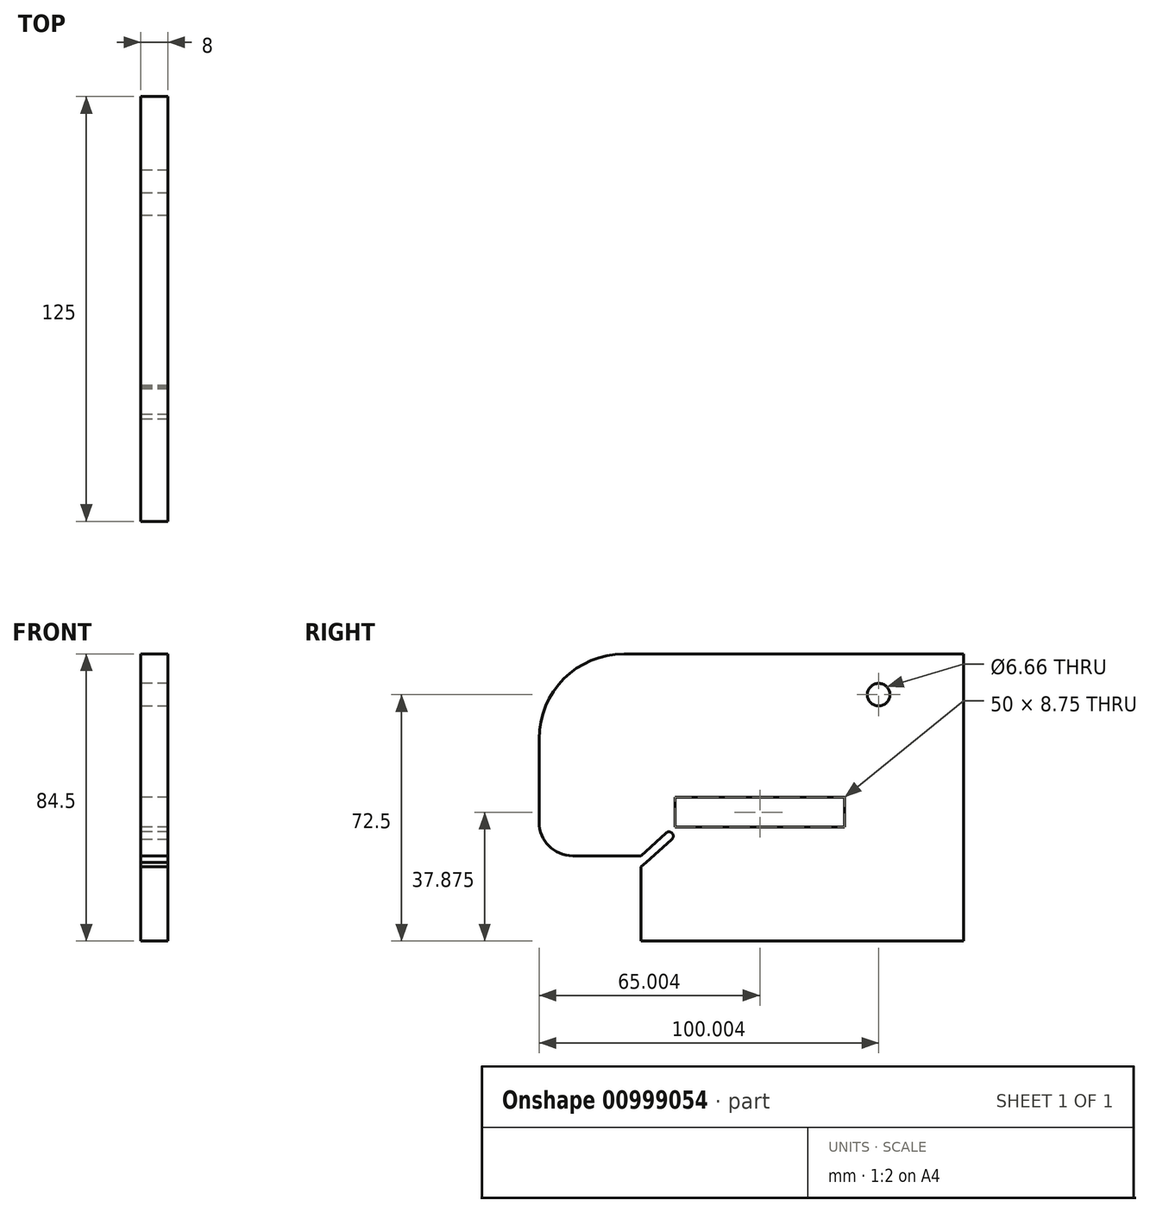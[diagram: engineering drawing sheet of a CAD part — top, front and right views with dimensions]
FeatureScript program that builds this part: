
annotation { "Feature Type Name" : "Feature", "Feature Type Description" : "" }
export const myFeature = defineFeature(function(context is Context, id is Id, definition is map)
    precondition{}
    {
        {
            var Q0;
            Q0=qCreatedBy(makeId("Right.planeOp"),FACE);
            var sketch = newSketch(context, id + "F0", { "sketchPlane" : qUnion([Q0])});
            skLineSegment(sketch, "E0", {"start": v(-19.9, 42.25) * mm, "end": v(42.6, 42.25) * mm});
            skLineSegment(sketch, "E1", {"start": v(42.6, 42.25) * mm, "end": v(42.6, 0) * mm});
            skLineSegment(sketch, "E2", {"start": v(42.6, 0) * mm, "end": v(42.6, -42.25) * mm});
            skLineSegment(sketch, "E3", {"start": v(42.6, -42.25) * mm, "end": v(-52.4, -42.25) * mm});
            skLineSegment(sketch, "E4", {"start": v(-52.4, -42.25) * mm, "end": v(-52.4, -20.38) * mm});
            skLineSegment(sketch, "E5", {"start": v(-52.4, -17.16) * mm, "end": v(-72.5, -17.16) * mm});
            skLineSegment(sketch, "E6", {"start": v(-82.4, -7.25) * mm, "end": v(-82.4, 17.25) * mm});
            skLineSegment(sketch, "E7", {"start": v(-57.4, 42.25) * mm, "end": v(-19.9, 42.25) * mm});
            skLineSegment(sketch, "E8", {"start": v(42.6, 42.25) * mm, "end": v(17.6, 42.25) * mm});
            skLineSegment(sketch, "E9", {"start": v(17.6, 42.25) * mm, "end": v(17.6, 30.25) * mm});
            skCircle(sketch, "E10", {"center": v(17.6, 30.25) * mm, "radius": 3.33 * mm});
            skPoint(sketch, "E11.visualSharp", {"position": v(-82.4, 42.25) * mm});
            skArc(sketch, "E11.filletArc", {"start": v(-57.4, 42.25) * mm, "mid": v(-75.08, 34.93) * mm, "end": v(-82.4, 17.25) * mm});
            skLineSegment(sketch, "E12", {"start": v(17.6, 30.25) * mm, "end": v(17.6, -8.75) * mm, "construction": true});
            skLineSegment(sketch, "E13", {"start": v(17.6, -8.75) * mm, "end": v(7.6, -8.75) * mm, "construction": true});
            skLineSegment(sketch, "E14", {"start": v(7.6, -8.75) * mm, "end": v(7.6, 0) * mm});
            skLineSegment(sketch, "E15", {"start": v(7.6, 0) * mm, "end": v(-42.4, 0) * mm});
            skLineSegment(sketch, "E16", {"start": v(-42.4, 0) * mm, "end": v(-42.4, -8.75) * mm});
            skLineSegment(sketch, "E17", {"start": v(-42.4, -8.75) * mm, "end": v(7.6, -8.75) * mm});
            skLineSegment(sketch, "E18", {"start": v(-52.4, -17.16) * mm, "end": v(-45, -10.44) * mm});
            skLineSegment(sketch, "E19.0", {"start": v(-50.9, -19.17) * mm, "end": v(-43.41, -12.38) * mm});
            skArc(sketch, "E20", {"start": v(-45, -10.44) * mm, "mid": v(-43.18, -10.58) * mm, "end": v(-43.41, -12.38) * mm});
            skLineSegment(sketch, "E21", {"start": v(-50.9, -19.17) * mm, "end": v(-52.4, -20.38) * mm});
            skPoint(sketch, "E22.visualSharp", {"position": v(-82.4, -17.16) * mm});
            skArc(sketch, "E22.filletArc", {"start": v(-82.4, -7.25) * mm, "mid": v(-79.5, -14.25) * mm, "end": v(-72.5, -17.16) * mm});
            skSolve(sketch);
        }
        {
            var Q0;
            {var subQ6=sQuery(id+"F0.wireOp",EDGE,"E1");Q0=makeQuery(id+"F0.imprint","IMPRINT",FACE,{"disambiguationData":[TD([[makeQuery(id+"F0.imprint","IMPRINT",EDGE,{"derivedFrom":subQ6}),-1.0]])]});}
            extrude(context, id + "F1", {"entities" : qUnion([Q0]), "depth" : 8 * mm, "offsetDistance" : 25 * mm});
        }
    });
